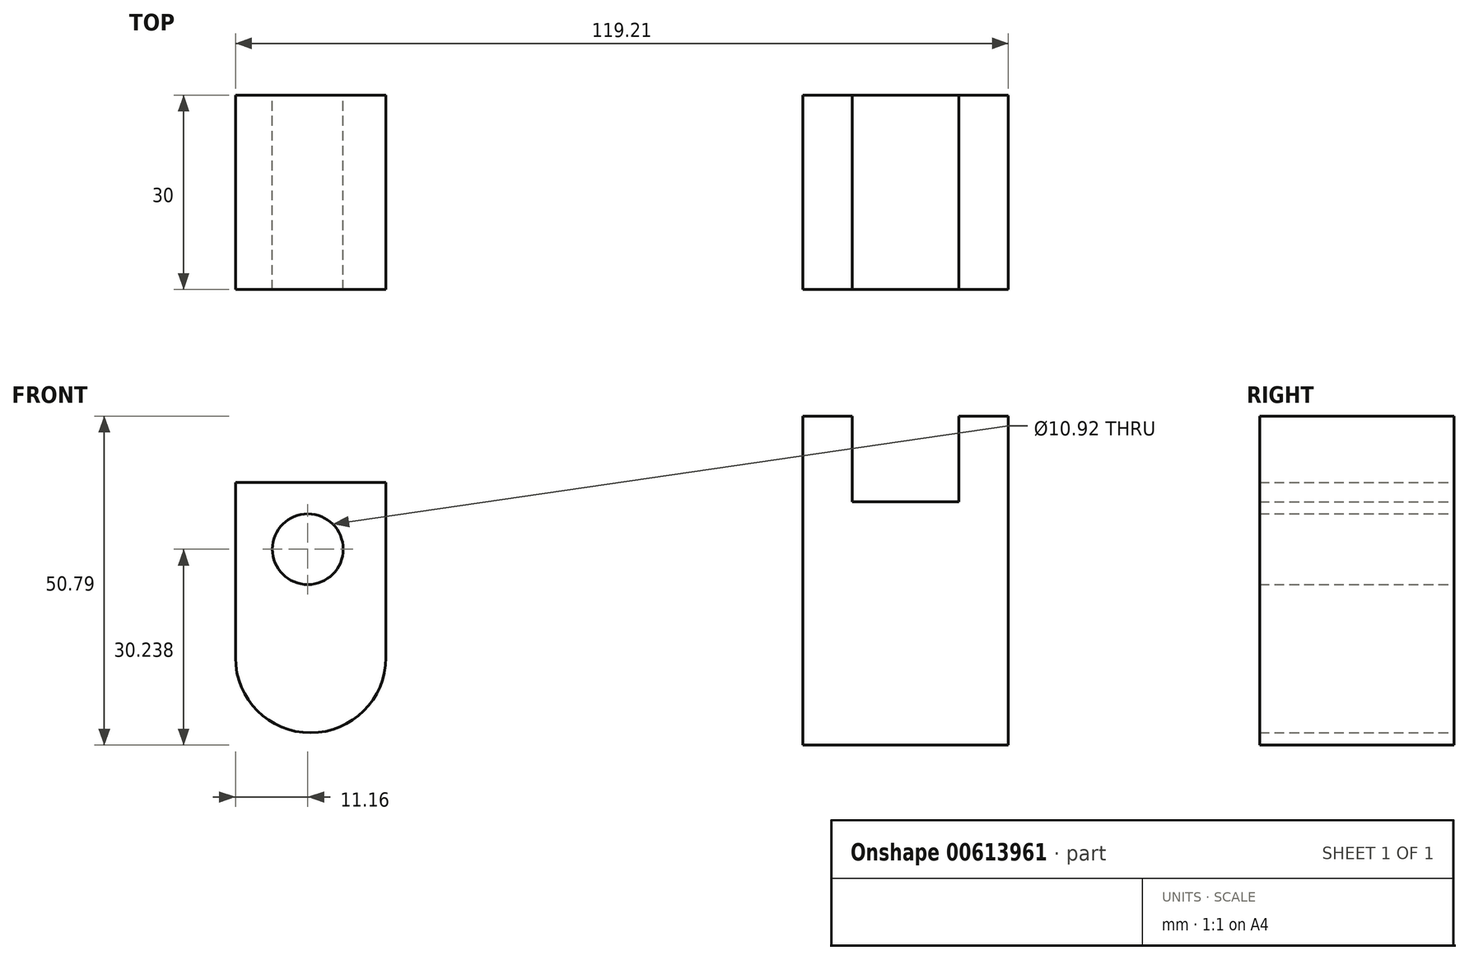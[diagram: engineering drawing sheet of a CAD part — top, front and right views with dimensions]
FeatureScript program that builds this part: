
annotation { "Feature Type Name" : "Feature", "Feature Type Description" : "" }
export const myFeature = defineFeature(function(context is Context, id is Id, definition is map)
    precondition{}
    {
        {
            var Q0;
            Q0=qCreatedBy(makeId("Front.planeOp"),FACE);
            var sketch = newSketch(context, id + "F0", { "sketchPlane" : qUnion([Q0])});
            skLineSegment(sketch, "E0.bottom", {"start": v(-59.46, 43.45) * mm, "end": v(-36.26, 43.45) * mm});
            skLineSegment(sketch, "E0.left", {"start": v(-59.46, 43.45) * mm, "end": v(-59.46, 16.44) * mm});
            skLineSegment(sketch, "E0.right", {"start": v(-36.26, 43.45) * mm, "end": v(-36.26, 16.44) * mm});
            skLineSegment(sketch, "E1.top", {"start": v(28.04, 2.94) * mm, "end": v(59.75, 2.94) * mm});
            skLineSegment(sketch, "E1.left", {"start": v(28.04, 32.88) * mm, "end": v(28.04, 2.94) * mm});
            skLineSegment(sketch, "E1.right", {"start": v(59.75, 32.88) * mm, "end": v(59.75, 2.94) * mm});
            skLineSegment(sketch, "E2.top", {"start": v(35.67, 40.52) * mm, "end": v(52.12, 40.52) * mm});
            skLineSegment(sketch, "E2.left", {"start": v(28.04, 32.88) * mm, "end": v(28.04, 40.52) * mm});
            skLineSegment(sketch, "E2.right", {"start": v(59.75, 32.88) * mm, "end": v(59.75, 40.52) * mm});
            skLineSegment(sketch, "E3.top", {"start": v(59.75, 53.73) * mm, "end": v(52.12, 53.73) * mm});
            skLineSegment(sketch, "E3.left", {"start": v(59.75, 40.52) * mm, "end": v(59.75, 53.73) * mm});
            skLineSegment(sketch, "E3.right", {"start": v(52.12, 40.52) * mm, "end": v(52.12, 53.73) * mm});
            skLineSegment(sketch, "E4.top", {"start": v(28.04, 53.73) * mm, "end": v(35.67, 53.73) * mm});
            skLineSegment(sketch, "E4.left", {"start": v(28.04, 40.52) * mm, "end": v(28.04, 53.73) * mm});
            skLineSegment(sketch, "E4.right", {"start": v(35.67, 40.52) * mm, "end": v(35.67, 53.73) * mm});
            skArc(sketch, "E5", {"start": v(-59.46, 16.44) * mm, "mid": v(-47.86, 4.84) * mm, "end": v(-36.26, 16.44) * mm});
            skCircle(sketch, "E6", {"center": v(-48.3, 33.18) * mm, "radius": 5.46 * mm});
            skSolve(sketch);
        }
        {
            var Q0;
            Q0 = qSketchRegion(id + "F0", true);
            extrude(context, id + "F1", {"entities" : qUnion([Q0]), "depth" : 30 * mm, "offsetDistance" : 25 * mm});
        }
    });
